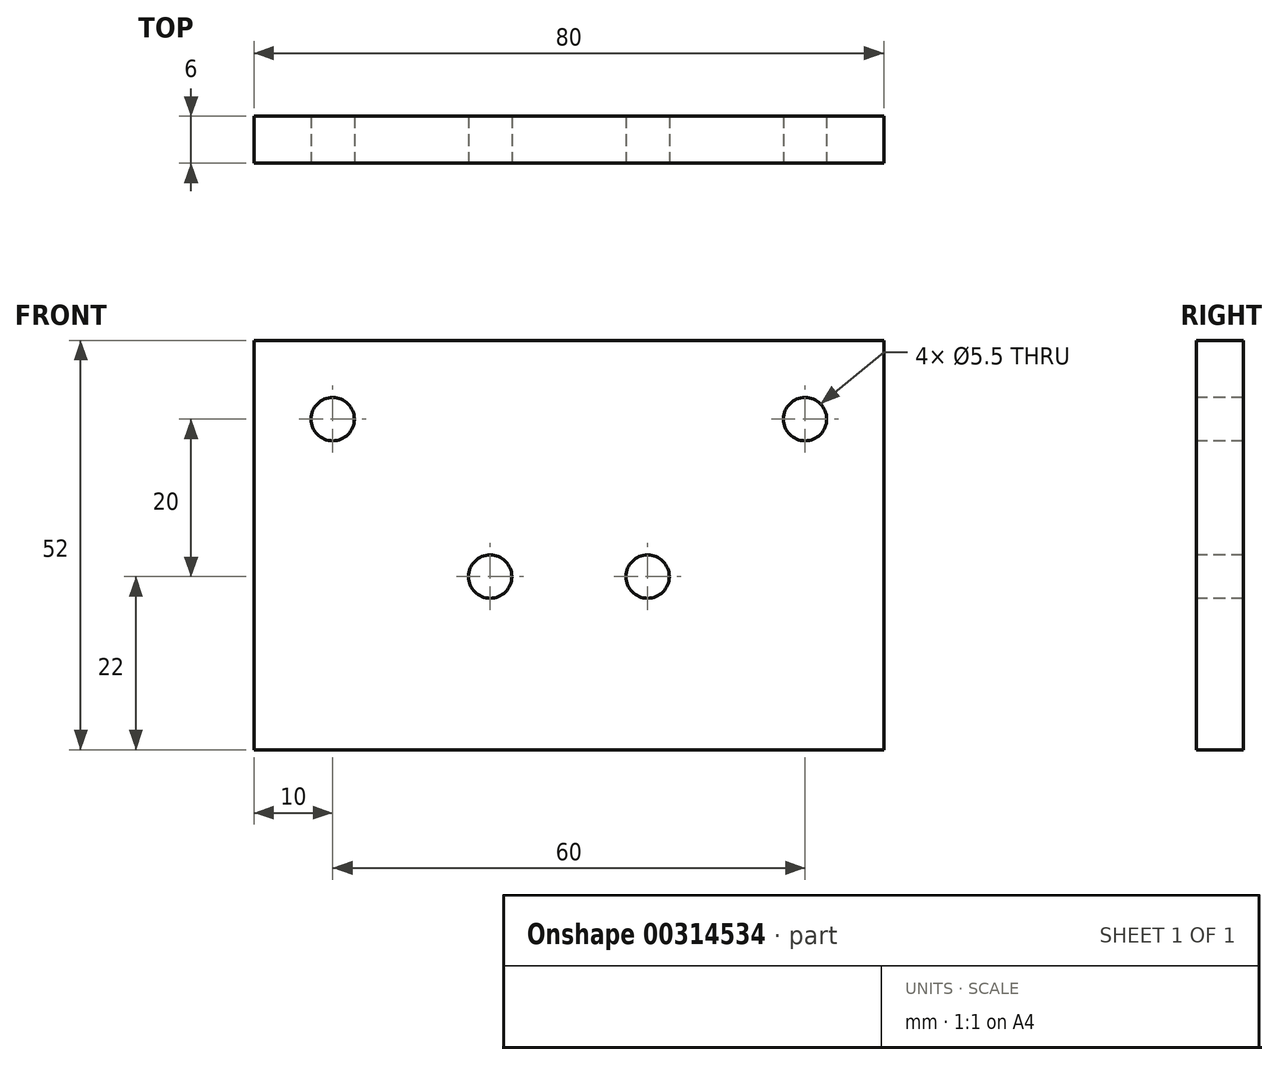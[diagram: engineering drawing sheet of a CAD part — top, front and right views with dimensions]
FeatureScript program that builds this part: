
annotation { "Feature Type Name" : "Feature", "Feature Type Description" : "" }
export const myFeature = defineFeature(function(context is Context, id is Id, definition is map)
    precondition{}
    {
        {
            var Q0;
            Q0=qCreatedBy(makeId("Front.planeOp"),FACE);
            var sketch = newSketch(context, id + "F0", { "sketchPlane" : qUnion([Q0])});
            skLineSegment(sketch, "E0.bottom", {"start": v(-40, -26) * mm, "end": v(40, -26) * mm});
            skLineSegment(sketch, "E0.left", {"start": v(-40, -26) * mm, "end": v(-40, 26) * mm});
            skLineSegment(sketch, "E0.right", {"start": v(40, -26) * mm, "end": v(40, 26) * mm});
            skPoint(sketch, "E0.middle", {"position": v(0, 0) * mm});
            skLineSegment(sketch, "E1", {"start": v(-40, 26) * mm, "end": v(40, 26) * mm});
            skSolve(sketch);
        }
        {
            var Q0;
            Q0=qSketchRegion(id+"F0",true);
            extrude(context, id + "F1", {"entities" : qUnion([Q0]), "depth" : 6 * mm});
        }
        {
            var Q0;
            Q0=makeQuery(id+"F1.opExtrude","CAP_FACE",FACE,{"disambiguationData":[OSD([sQuery(id+"F0.wireOp",EDGE,"E0.bottom"),sQuery(id+"F0.wireOp",EDGE,"E0.top"),sQuery(id+"F0.wireOp",EDGE,"E0.left"),sQuery(id+"F0.wireOp",EDGE,"E0.right"),sQuery(id+"F0.wireOp",EDGE,"stzXivqM-I9MG-fgFX-9sOb-lYkelWrfb2BA.top"),sQuery(id+"F0.wireOp",EDGE,"stzXivqM-I9MG-fgFX-9sOb-lYkelWrfb2BA.left"),sQuery(id+"F0.wireOp",EDGE,"stzXivqM-I9MG-fgFX-9sOb-lYkelWrfb2BA.right"),sQuery(id+"F0.wireOp",EDGE,"1328e53c-2e2d-4420-a0af-21f9c98d15e1.trimOffspring")])],"isStart":false});
            var sketch = newSketch(context, id + "F2", { "sketchPlane" : qUnion([Q0])});
            skPoint(sketch, "E2", {"position": v(-30, 16) * mm});
            skPoint(sketch, "E3.MirrorP", {"position": v(30, 16) * mm});
            skPoint(sketch, "E4", {"position": v(-10, -4) * mm});
            skPoint(sketch, "E5.MirrorP", {"position": v(10, -4) * mm});
            skSolve(sketch);
        }
        {
            var Q0;
            Q0=sQuery(id+"F2.wireOp",VERTEX,"E2");
            var Q1;
            Q1=sQuery(id+"F2.wireOp",VERTEX,"E4");
            var Q2;
            Q2=sQuery(id+"F2.wireOp",VERTEX,"E5.MirrorP");
            var Q3;
            Q3=sQuery(id+"F2.wireOp",VERTEX,"E3.MirrorP");
            var Q4;
            Q4=makeQuery(id+"F1.opExtrude","SWEPT_BODY",BODY,{"disambiguationData":[OSD([sQuery(id+"F0.wireOp",EDGE,"E0.bottom"),sQuery(id+"F0.wireOp",EDGE,"E0.top"),sQuery(id+"F0.wireOp",EDGE,"E0.left"),sQuery(id+"F0.wireOp",EDGE,"E0.right"),sQuery(id+"F0.wireOp",EDGE,"stzXivqM-I9MG-fgFX-9sOb-lYkelWrfb2BA.top"),sQuery(id+"F0.wireOp",EDGE,"stzXivqM-I9MG-fgFX-9sOb-lYkelWrfb2BA.left"),sQuery(id+"F0.wireOp",EDGE,"stzXivqM-I9MG-fgFX-9sOb-lYkelWrfb2BA.right"),sQuery(id+"F0.wireOp",EDGE,"1328e53c-2e2d-4420-a0af-21f9c98d15e1.trimOffspring")])]});
            hole(context, id + "F3", {"style" : HoleStyle.SIMPLE, "endStyle" : HoleEndStyle.THROUGH, "standardTappedOrClearance" : lookupTablePath({ "standard" : "ISO", "fit" : "Normal", "size" : "M5", "type" : "Clearance" }), "standardBlindInLast" : lookupTablePath({ "fit" : "Standard", "standard" : "ISO", "size" : "M5", "type" : "Clearance" }), "holeDiameter" : 5.5 * mm, "tappedDepth" : 12 * mm, "tapClearance" : 3, "locations" : qUnion([Q0, Q1, Q2, Q3]), "scope" : qUnion([Q4])});
        }
    });
